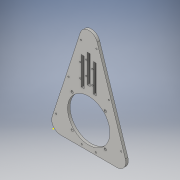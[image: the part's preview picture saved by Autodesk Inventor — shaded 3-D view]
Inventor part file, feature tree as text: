
AUTODESK INVENTOR PART (.ipt)
format: ipt  version: 2016 (Build 200138000, 138)  size: 214,528 bytes
history: native  units: in
note: dims shown in document units (in); Inventor stores cm internally (conversion verified against a paired STEP export)
features: sketch x3, extrude x3
ambient origin geometry x8: Origin, YZ Plane, XZ Plane, XY Plane, X Axis, Y Axis, Z Axis, Center Point
bodies: Body1 (feature_tree)
feature tree (6):
  sketch  "Sketch1"  dims[d12=0.25in d13=3.0in d14=0.166in d15=0.166in d16=0.166in d17=0.166in d18=0.15in d19=0.75in d20=0.75in d21=1.9in d22=1.9in d25=1.25in]
  extrude  "Extrusion3"  Depth=1.25in
  extrude  "Extrusion11"  Depth=1.25in
  sketch  "Sketch3"  dims[d30=1.0in d31=1.0in d32=1.0in d33=0.4in d34=0.4in d35=0.05in d37=0.05in d38=0.18in d39=0.0in d40=0.4in d41=0.4in d42=0.1in d43=0.1in d44=0.1in d45=0.1in d183=0.2in d184=2.0in d185=0.143in d186=0.22in d189=0.105in d194=0.2in d196=0.143in d197=0.22in d198=2.0in d199=0.0713in d203=0.105in d204=0.105in d205=0.0713in d207=1.643in d208=0.643in d209=0.0713in d211=0.2in d212=2.0in d216=0.105in d217=0.105in d218=0.18in d219=0.0in d221=0.175in d222=0.2in d224=0.2in d225=0.15in d226=0.18in d227=0.0in d228=1.5in d229=1.5in]
  extrude  "Extrusion12"  Depth=1.5in
  sketch  "Sketch2"  dims[d26=1.25in d27=1.25in]
